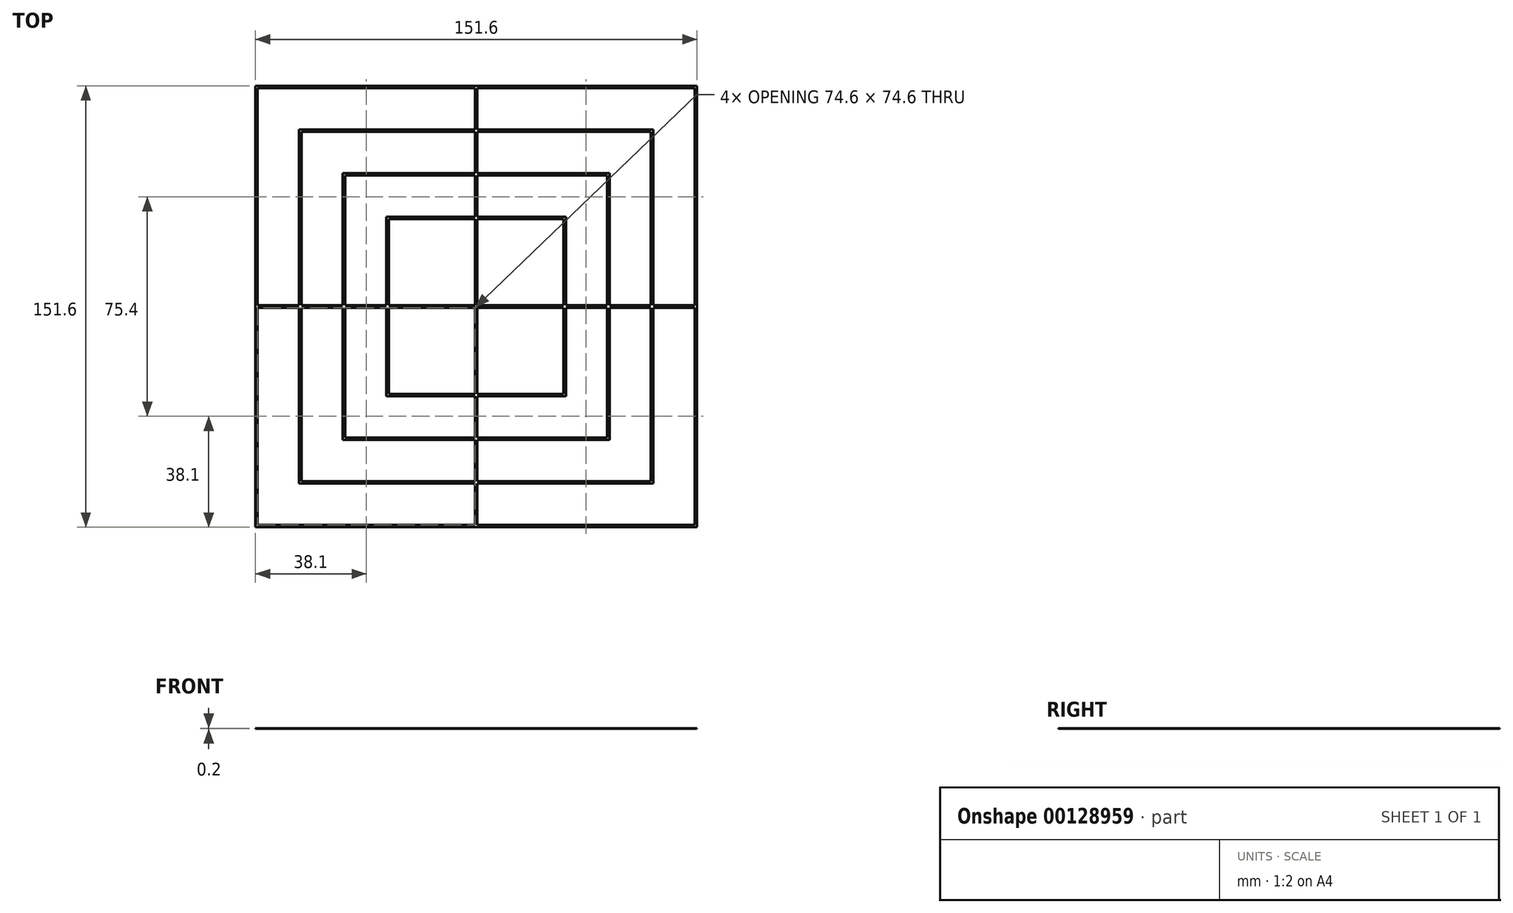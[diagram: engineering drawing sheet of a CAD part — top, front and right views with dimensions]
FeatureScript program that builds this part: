
annotation { "Feature Type Name" : "Feature", "Feature Type Description" : "" }
export const myFeature = defineFeature(function(context is Context, id is Id, definition is map)
    precondition{}
    {
        {
            var Q0;
            Q0=qCreatedBy(makeId("Top.planeOp"),FACE);
            var sketch = newSketch(context, id + "F0", { "sketchPlane" : qUnion([Q0])});
            skLineSegment(sketch, "E0.bottom", {"start": v(75, -75) * mm, "end": v(-75, -75) * mm});
            skLineSegment(sketch, "E0.top", {"start": v(75, 75) * mm, "end": v(-75, 75) * mm});
            skLineSegment(sketch, "E0.left", {"start": v(75, -75) * mm, "end": v(75, 75) * mm});
            skLineSegment(sketch, "E0.right", {"start": v(-75, -75) * mm, "end": v(-75, 75) * mm});
            skPoint(sketch, "E0.middle", {"position": v(0, 0) * mm});
            skLineSegment(sketch, "E1.bottom", {"start": v(60, -60) * mm, "end": v(-60, -60) * mm});
            skLineSegment(sketch, "E1.top", {"start": v(60, 60) * mm, "end": v(-60, 60) * mm});
            skLineSegment(sketch, "E1.left", {"start": v(60, -60) * mm, "end": v(60, 60) * mm});
            skLineSegment(sketch, "E1.right", {"start": v(-60, -60) * mm, "end": v(-60, 60) * mm});
            skLineSegment(sketch, "E2.bottom", {"start": v(45, -45) * mm, "end": v(-45, -45) * mm});
            skLineSegment(sketch, "E2.top", {"start": v(45, 45) * mm, "end": v(-45, 45) * mm});
            skLineSegment(sketch, "E2.left", {"start": v(45, -45) * mm, "end": v(45, 45) * mm});
            skLineSegment(sketch, "E2.right", {"start": v(-45, -45) * mm, "end": v(-45, 45) * mm});
            skLineSegment(sketch, "E3.bottom", {"start": v(30, -30) * mm, "end": v(-30, -30) * mm});
            skLineSegment(sketch, "E3.top", {"start": v(30, 30) * mm, "end": v(-30, 30) * mm});
            skLineSegment(sketch, "E3.left", {"start": v(30, -30) * mm, "end": v(30, 30) * mm});
            skLineSegment(sketch, "E3.right", {"start": v(-30, -30) * mm, "end": v(-30, 30) * mm});
            skLineSegment(sketch, "E4", {"start": v(-75, 0) * mm, "end": v(75, 0) * mm});
            skLineSegment(sketch, "E5", {"start": v(0, 75) * mm, "end": v(0, -75) * mm});
            skLineSegment(sketch, "E6.bottom", {"start": v(75.8, -75.8) * mm, "end": v(-75.8, -75.8) * mm});
            skLineSegment(sketch, "E6.top", {"start": v(75.8, 75.8) * mm, "end": v(-75.8, 75.8) * mm});
            skLineSegment(sketch, "E6.left", {"start": v(75.8, -75.8) * mm, "end": v(75.8, 75.8) * mm});
            skLineSegment(sketch, "E6.right", {"start": v(-75.8, -75.8) * mm, "end": v(-75.8, 75.8) * mm});
            skLineSegment(sketch, "E7.bottom", {"start": v(60.8, -60.8) * mm, "end": v(-60.8, -60.8) * mm});
            skLineSegment(sketch, "E7.top", {"start": v(60.8, 60.8) * mm, "end": v(-60.8, 60.8) * mm});
            skLineSegment(sketch, "E7.left", {"start": v(60.8, -60.8) * mm, "end": v(60.8, 60.8) * mm});
            skLineSegment(sketch, "E7.right", {"start": v(-60.8, -60.8) * mm, "end": v(-60.8, 60.8) * mm});
            skLineSegment(sketch, "E8.bottom", {"start": v(45.8, -45.8) * mm, "end": v(-45.8, -45.8) * mm});
            skLineSegment(sketch, "E8.top", {"start": v(45.8, 45.8) * mm, "end": v(-45.8, 45.8) * mm});
            skLineSegment(sketch, "E8.left", {"start": v(45.8, -45.8) * mm, "end": v(45.8, 45.8) * mm});
            skLineSegment(sketch, "E8.right", {"start": v(-45.8, -45.8) * mm, "end": v(-45.8, 45.8) * mm});
            skLineSegment(sketch, "E9.bottom", {"start": v(30.8, -30.8) * mm, "end": v(-30.8, -30.8) * mm});
            skLineSegment(sketch, "E9.top", {"start": v(30.8, 30.8) * mm, "end": v(-30.8, 30.8) * mm});
            skLineSegment(sketch, "E9.left", {"start": v(30.8, -30.8) * mm, "end": v(30.8, 30.8) * mm});
            skLineSegment(sketch, "E9.right", {"start": v(-30.8, -30.8) * mm, "end": v(-30.8, 30.8) * mm});
            skLineSegment(sketch, "E10", {"start": v(-75, -0.4) * mm, "end": v(75, -0.4) * mm});
            skLineSegment(sketch, "E11.MirrorCS", {"start": v(-75, 0.4) * mm, "end": v(75, 0.4) * mm});
            skLineSegment(sketch, "E12", {"start": v(-0.4, 75) * mm, "end": v(-0.4, -75) * mm});
            skLineSegment(sketch, "E13.MirrorCS", {"start": v(0.4, 75) * mm, "end": v(0.4, -75) * mm});
            skSolve(sketch);
        }
        {
            var Q0;
            {var subQ5=sQuery(id+"F0.wireOp",EDGE,"E3.right");var subQ6=sQuery(id+"F0.wireOp",EDGE,"E3.top");var subQ7=makeQuery(id+"F0.imprint","INTERSECT",VERTEX,{"derivedFrom":[subQ6,subQ5]});Q0=makeQuery(id+"F0.imprint","IMPRINT",FACE,{"disambiguationData":[TD([[makeQuery(id+"F0.imprint","IMPRINT",EDGE,{"disambiguationData":[TD([[subQ7,1.0]])],"derivedFrom":subQ6}),-1.0]])]});}
            var Q1;
            {var subQ6=sQuery(id+"F0.wireOp",EDGE,"E1.right");var subQ9=sQuery(id+"F0.wireOp",EDGE,"E1.top");var subQ10=makeQuery(id+"F0.imprint","INTERSECT",VERTEX,{"derivedFrom":[subQ9,subQ6]});Q1=makeQuery(id+"F0.imprint","IMPRINT",FACE,{"disambiguationData":[TD([[makeQuery(id+"F0.imprint","IMPRINT",EDGE,{"disambiguationData":[TD([[subQ10,1.0]])],"derivedFrom":subQ9}),-1.0]])]});}
            var Q2;
            {var subQ5=sQuery(id+"F0.wireOp",EDGE,"E2.right");var subQ6=sQuery(id+"F0.wireOp",EDGE,"E2.top");var subQ7=makeQuery(id+"F0.imprint","INTERSECT",VERTEX,{"derivedFrom":[subQ6,subQ5]});Q2=makeQuery(id+"F0.imprint","IMPRINT",FACE,{"disambiguationData":[TD([[makeQuery(id+"F0.imprint","IMPRINT",EDGE,{"disambiguationData":[TD([[subQ7,1.0]])],"derivedFrom":subQ6}),-1.0]])]});}
            var Q3;
            {var subQ5=sQuery(id+"F0.wireOp",EDGE,"E3.right");var subQ6=sQuery(id+"F0.wireOp",EDGE,"E3.bottom");var subQ7=makeQuery(id+"F0.imprint","INTERSECT",VERTEX,{"derivedFrom":[subQ6,subQ5]});Q3=makeQuery(id+"F0.imprint","IMPRINT",FACE,{"disambiguationData":[TD([[makeQuery(id+"F0.imprint","IMPRINT",EDGE,{"disambiguationData":[TD([[subQ7,1.0]])],"derivedFrom":subQ6}),1.0]])]});}
            var Q4;
            {var subQ7=sQuery(id+"F0.wireOp",EDGE,"E3.left");var subQ8=sQuery(id+"F0.wireOp",EDGE,"E3.top");var subQ9=makeQuery(id+"F0.imprint","INTERSECT",VERTEX,{"derivedFrom":[subQ8,subQ7]});Q4=makeQuery(id+"F0.imprint","IMPRINT",FACE,{"disambiguationData":[TD([[makeQuery(id+"F0.imprint","IMPRINT",EDGE,{"disambiguationData":[TD([[subQ9,-1.0]])],"derivedFrom":subQ8}),-1.0]])]});}
            var Q5;
            {var subQ7=sQuery(id+"F0.wireOp",EDGE,"E2.left");var subQ9=sQuery(id+"F0.wireOp",EDGE,"E2.top");var subQ10=makeQuery(id+"F0.imprint","INTERSECT",VERTEX,{"derivedFrom":[subQ9,subQ7]});Q5=makeQuery(id+"F0.imprint","IMPRINT",FACE,{"disambiguationData":[TD([[makeQuery(id+"F0.imprint","IMPRINT",EDGE,{"disambiguationData":[TD([[subQ10,-1.0]])],"derivedFrom":subQ9}),-1.0]])]});}
            var Q6;
            {var subQ7=sQuery(id+"F0.wireOp",EDGE,"E3.left");var subQ8=sQuery(id+"F0.wireOp",EDGE,"E3.bottom");var subQ9=makeQuery(id+"F0.imprint","INTERSECT",VERTEX,{"derivedFrom":[subQ8,subQ7]});Q6=makeQuery(id+"F0.imprint","IMPRINT",FACE,{"disambiguationData":[TD([[makeQuery(id+"F0.imprint","IMPRINT",EDGE,{"disambiguationData":[TD([[subQ9,-1.0]])],"derivedFrom":subQ8}),1.0]])]});}
            var Q7;
            {var subQ5=sQuery(id+"F0.wireOp",EDGE,"E1.left");var subQ6=sQuery(id+"F0.wireOp",EDGE,"E1.bottom");var subQ7=makeQuery(id+"F0.imprint","INTERSECT",VERTEX,{"derivedFrom":[subQ6,subQ5]});Q7=makeQuery(id+"F0.imprint","IMPRINT",FACE,{"disambiguationData":[TD([[makeQuery(id+"F0.imprint","IMPRINT",EDGE,{"disambiguationData":[TD([[subQ7,-1.0]])],"derivedFrom":subQ6}),1.0]])]});}
            var Q8;
            {var subQ0=sQuery(id+"F0.wireOp",EDGE,"E1.right");var subQ1=sQuery(id+"F0.wireOp",EDGE,"E1.bottom");var subQ2=makeQuery(id+"F0.imprint","INTERSECT",VERTEX,{"derivedFrom":[subQ1,subQ0]});Q8=makeQuery(id+"F0.imprint","IMPRINT",FACE,{"disambiguationData":[TD([[makeQuery(id+"F0.imprint","IMPRINT",EDGE,{"disambiguationData":[TD([[subQ2,1.0]])],"derivedFrom":subQ1}),1.0]])]});}
            var Q9;
            Q9=makeQuery(id+"F0.imprint","IMPRINT",FACE,{"disambiguationData":[TD([[makeQuery(id+"F0.imprint","IMPRINT",EDGE,{"derivedFrom":sQuery(id+"F0.wireOp",EDGE,"E6.bottom")}),-1.0]])]});
            var Q10;
            {var subQ7=sQuery(id+"F0.wireOp",EDGE,"E1.left");var subQ8=sQuery(id+"F0.wireOp",EDGE,"E1.top");var subQ9=makeQuery(id+"F0.imprint","INTERSECT",VERTEX,{"derivedFrom":[subQ8,subQ7]});Q10=makeQuery(id+"F0.imprint","IMPRINT",FACE,{"disambiguationData":[TD([[makeQuery(id+"F0.imprint","IMPRINT",EDGE,{"disambiguationData":[TD([[subQ9,-1.0]])],"derivedFrom":subQ8}),-1.0]])]});}
            var Q11;
            {var subQ0=sQuery(id+"F0.wireOp",EDGE,"E10");var subQ1=sQuery(id+"F0.wireOp",EDGE,"E1.right");var subQ2=makeQuery(id+"F0.imprint","INTERSECT",VERTEX,{"derivedFrom":[subQ1,subQ0]});Q11=makeQuery(id+"F0.imprint","IMPRINT",FACE,{"disambiguationData":[TD([[makeQuery(id+"F0.imprint","IMPRINT",EDGE,{"disambiguationData":[TD([[subQ2,-1.0]])],"derivedFrom":subQ1}),-1.0]])]});}
            var Q12;
            {var subQ0=sQuery(id+"F0.wireOp",EDGE,"E4");var subQ1=sQuery(id+"F0.wireOp",EDGE,"E3.left");var subQ2=makeQuery(id+"F0.imprint","INTERSECT",VERTEX,{"derivedFrom":[subQ1,subQ0]});Q12=makeQuery(id+"F0.imprint","IMPRINT",FACE,{"disambiguationData":[TD([[makeQuery(id+"F0.imprint","IMPRINT",EDGE,{"disambiguationData":[TD([[subQ2,-1.0]])],"derivedFrom":subQ1}),1.0]])]});}
            var Q13;
            {var subQ5=sQuery(id+"F0.wireOp",EDGE,"E2.right");var subQ6=sQuery(id+"F0.wireOp",EDGE,"E2.bottom");var subQ7=makeQuery(id+"F0.imprint","INTERSECT",VERTEX,{"derivedFrom":[subQ6,subQ5]});Q13=makeQuery(id+"F0.imprint","IMPRINT",FACE,{"disambiguationData":[TD([[makeQuery(id+"F0.imprint","IMPRINT",EDGE,{"disambiguationData":[TD([[subQ7,1.0]])],"derivedFrom":subQ6}),1.0]])]});}
            var Q14;
            {var subQ0=sQuery(id+"F0.wireOp",EDGE,"E4");var subQ1=sQuery(id+"F0.wireOp",EDGE,"E2.right");var subQ2=makeQuery(id+"F0.imprint","INTERSECT",VERTEX,{"derivedFrom":[subQ1,subQ0]});Q14=makeQuery(id+"F0.imprint","IMPRINT",FACE,{"disambiguationData":[TD([[makeQuery(id+"F0.imprint","IMPRINT",EDGE,{"disambiguationData":[TD([[subQ2,-1.0]])],"derivedFrom":subQ1}),1.0]])]});}
            var Q15;
            {var subQ0=sQuery(id+"F0.wireOp",EDGE,"E10");var subQ1=sQuery(id+"F0.wireOp",EDGE,"E1.left");var subQ2=makeQuery(id+"F0.imprint","INTERSECT",VERTEX,{"derivedFrom":[subQ1,subQ0]});Q15=makeQuery(id+"F0.imprint","IMPRINT",FACE,{"disambiguationData":[TD([[makeQuery(id+"F0.imprint","IMPRINT",EDGE,{"disambiguationData":[TD([[subQ2,-1.0]])],"derivedFrom":subQ1}),1.0]])]});}
            var Q16;
            {var subQ0=sQuery(id+"F0.wireOp",EDGE,"E10");var subQ1=sQuery(id+"F0.wireOp",EDGE,"E1.right");var subQ2=makeQuery(id+"F0.imprint","INTERSECT",VERTEX,{"derivedFrom":[subQ1,subQ0]});Q16=makeQuery(id+"F0.imprint","IMPRINT",FACE,{"disambiguationData":[TD([[makeQuery(id+"F0.imprint","IMPRINT",EDGE,{"disambiguationData":[TD([[subQ2,-1.0]])],"derivedFrom":subQ1}),1.0]])]});}
            var Q17;
            {var subQ0=sQuery(id+"F0.wireOp",EDGE,"E10");var subQ1=sQuery(id+"F0.wireOp",EDGE,"E2.right");var subQ2=makeQuery(id+"F0.imprint","INTERSECT",VERTEX,{"derivedFrom":[subQ1,subQ0]});Q17=makeQuery(id+"F0.imprint","IMPRINT",FACE,{"disambiguationData":[TD([[makeQuery(id+"F0.imprint","IMPRINT",EDGE,{"disambiguationData":[TD([[subQ2,-1.0]])],"derivedFrom":subQ1}),-1.0]])]});}
            var Q18;
            {var subQ0=sQuery(id+"F0.wireOp",EDGE,"E4");var subQ1=sQuery(id+"F0.wireOp",EDGE,"E0.left");var subQ2=makeQuery(id+"F0.imprint","INTERSECT",VERTEX,{"derivedFrom":[subQ1,subQ0]});Q18=makeQuery(id+"F0.imprint","IMPRINT",FACE,{"disambiguationData":[TD([[makeQuery(id+"F0.imprint","IMPRINT",EDGE,{"disambiguationData":[TD([[subQ2,-1.0]])],"derivedFrom":subQ1}),1.0]])]});}
            var Q19;
            {var subQ0=sQuery(id+"F0.wireOp",EDGE,"E4");var subQ1=sQuery(id+"F0.wireOp",EDGE,"E0.right");var subQ2=makeQuery(id+"F0.imprint","INTERSECT",VERTEX,{"derivedFrom":[subQ1,subQ0]});Q19=makeQuery(id+"F0.imprint","IMPRINT",FACE,{"disambiguationData":[TD([[makeQuery(id+"F0.imprint","IMPRINT",EDGE,{"disambiguationData":[TD([[subQ2,-1.0]])],"derivedFrom":subQ1}),-1.0]])]});}
            var Q20;
            {var subQ0=sQuery(id+"F0.wireOp",EDGE,"E10");var subQ1=sQuery(id+"F0.wireOp",EDGE,"E3.left");var subQ2=makeQuery(id+"F0.imprint","INTERSECT",VERTEX,{"derivedFrom":[subQ1,subQ0]});Q20=makeQuery(id+"F0.imprint","IMPRINT",FACE,{"disambiguationData":[TD([[makeQuery(id+"F0.imprint","IMPRINT",EDGE,{"disambiguationData":[TD([[subQ2,-1.0]])],"derivedFrom":subQ1}),-1.0]])]});}
            var Q21;
            {var subQ0=sQuery(id+"F0.wireOp",EDGE,"E4");var subQ1=sQuery(id+"F0.wireOp",EDGE,"E1.right");var subQ2=makeQuery(id+"F0.imprint","INTERSECT",VERTEX,{"derivedFrom":[subQ1,subQ0]});Q21=makeQuery(id+"F0.imprint","IMPRINT",FACE,{"disambiguationData":[TD([[makeQuery(id+"F0.imprint","IMPRINT",EDGE,{"disambiguationData":[TD([[subQ2,-1.0]])],"derivedFrom":subQ1}),1.0]])]});}
            var Q22;
            {var subQ0=sQuery(id+"F0.wireOp",EDGE,"E4");var subQ1=sQuery(id+"F0.wireOp",EDGE,"E1.right");var subQ2=makeQuery(id+"F0.imprint","INTERSECT",VERTEX,{"derivedFrom":[subQ1,subQ0]});Q22=makeQuery(id+"F0.imprint","IMPRINT",FACE,{"disambiguationData":[TD([[makeQuery(id+"F0.imprint","IMPRINT",EDGE,{"disambiguationData":[TD([[subQ2,-1.0]])],"derivedFrom":subQ1}),-1.0]])]});}
            var Q23;
            {var subQ0=sQuery(id+"F0.wireOp",EDGE,"E4");var subQ1=sQuery(id+"F0.wireOp",EDGE,"E2.left");var subQ2=makeQuery(id+"F0.imprint","INTERSECT",VERTEX,{"derivedFrom":[subQ1,subQ0]});Q23=makeQuery(id+"F0.imprint","IMPRINT",FACE,{"disambiguationData":[TD([[makeQuery(id+"F0.imprint","IMPRINT",EDGE,{"disambiguationData":[TD([[subQ2,-1.0]])],"derivedFrom":subQ1}),1.0]])]});}
            var Q24;
            {var subQ0=sQuery(id+"F0.wireOp",EDGE,"E4");var subQ1=sQuery(id+"F0.wireOp",EDGE,"E1.left");var subQ2=makeQuery(id+"F0.imprint","INTERSECT",VERTEX,{"derivedFrom":[subQ1,subQ0]});Q24=makeQuery(id+"F0.imprint","IMPRINT",FACE,{"disambiguationData":[TD([[makeQuery(id+"F0.imprint","IMPRINT",EDGE,{"disambiguationData":[TD([[subQ2,-1.0]])],"derivedFrom":subQ1}),-1.0]])]});}
            var Q25;
            {var subQ0=sQuery(id+"F0.wireOp",EDGE,"E4");var subQ1=sQuery(id+"F0.wireOp",EDGE,"E3.right");var subQ2=makeQuery(id+"F0.imprint","INTERSECT",VERTEX,{"derivedFrom":[subQ1,subQ0]});Q25=makeQuery(id+"F0.imprint","IMPRINT",FACE,{"disambiguationData":[TD([[makeQuery(id+"F0.imprint","IMPRINT",EDGE,{"disambiguationData":[TD([[subQ2,-1.0]])],"derivedFrom":subQ1}),-1.0]])]});}
            var Q26;
            {var subQ5=sQuery(id+"F0.wireOp",EDGE,"E2.left");var subQ6=sQuery(id+"F0.wireOp",EDGE,"E2.bottom");var subQ7=makeQuery(id+"F0.imprint","INTERSECT",VERTEX,{"derivedFrom":[subQ6,subQ5]});Q26=makeQuery(id+"F0.imprint","IMPRINT",FACE,{"disambiguationData":[TD([[makeQuery(id+"F0.imprint","IMPRINT",EDGE,{"disambiguationData":[TD([[subQ7,-1.0]])],"derivedFrom":subQ6}),1.0]])]});}
            var Q27;
            {var subQ0=sQuery(id+"F0.wireOp",EDGE,"E4");var subQ1=sQuery(id+"F0.wireOp",EDGE,"E1.left");var subQ2=makeQuery(id+"F0.imprint","INTERSECT",VERTEX,{"derivedFrom":[subQ1,subQ0]});Q27=makeQuery(id+"F0.imprint","IMPRINT",FACE,{"disambiguationData":[TD([[makeQuery(id+"F0.imprint","IMPRINT",EDGE,{"disambiguationData":[TD([[subQ2,-1.0]])],"derivedFrom":subQ1}),1.0]])]});}
            var Q28;
            {var subQ0=sQuery(id+"F0.wireOp",EDGE,"E4");var subQ1=sQuery(id+"F0.wireOp",EDGE,"E2.right");var subQ2=makeQuery(id+"F0.imprint","INTERSECT",VERTEX,{"derivedFrom":[subQ1,subQ0]});Q28=makeQuery(id+"F0.imprint","IMPRINT",FACE,{"disambiguationData":[TD([[makeQuery(id+"F0.imprint","IMPRINT",EDGE,{"disambiguationData":[TD([[subQ2,-1.0]])],"derivedFrom":subQ1}),-1.0]])]});}
            var Q29;
            {var subQ0=sQuery(id+"F0.wireOp",EDGE,"E5");var subQ1=sQuery(id+"F0.wireOp",EDGE,"E0.bottom");var subQ2=makeQuery(id+"F0.imprint","INTERSECT",VERTEX,{"derivedFrom":[subQ1,subQ0]});Q29=makeQuery(id+"F0.imprint","IMPRINT",FACE,{"disambiguationData":[TD([[makeQuery(id+"F0.imprint","IMPRINT",EDGE,{"disambiguationData":[TD([[subQ2,1.0]])],"derivedFrom":subQ1}),-1.0]])]});}
            var Q30;
            {var subQ0=sQuery(id+"F0.wireOp",EDGE,"E4");var subQ1=sQuery(id+"F0.wireOp",EDGE,"E2.left");var subQ2=makeQuery(id+"F0.imprint","INTERSECT",VERTEX,{"derivedFrom":[subQ1,subQ0]});Q30=makeQuery(id+"F0.imprint","IMPRINT",FACE,{"disambiguationData":[TD([[makeQuery(id+"F0.imprint","IMPRINT",EDGE,{"disambiguationData":[TD([[subQ2,-1.0]])],"derivedFrom":subQ1}),-1.0]])]});}
            var Q31;
            {var subQ0=sQuery(id+"F0.wireOp",EDGE,"E10");var subQ1=sQuery(id+"F0.wireOp",EDGE,"E2.right");var subQ2=makeQuery(id+"F0.imprint","INTERSECT",VERTEX,{"derivedFrom":[subQ1,subQ0]});Q31=makeQuery(id+"F0.imprint","IMPRINT",FACE,{"disambiguationData":[TD([[makeQuery(id+"F0.imprint","IMPRINT",EDGE,{"disambiguationData":[TD([[subQ2,-1.0]])],"derivedFrom":subQ1}),1.0]])]});}
            var Q32;
            {var subQ0=sQuery(id+"F0.wireOp",EDGE,"E10");var subQ1=sQuery(id+"F0.wireOp",EDGE,"E3.left");var subQ2=makeQuery(id+"F0.imprint","INTERSECT",VERTEX,{"derivedFrom":[subQ1,subQ0]});Q32=makeQuery(id+"F0.imprint","IMPRINT",FACE,{"disambiguationData":[TD([[makeQuery(id+"F0.imprint","IMPRINT",EDGE,{"disambiguationData":[TD([[subQ2,-1.0]])],"derivedFrom":subQ1}),1.0]])]});}
            var Q33;
            {var subQ0=sQuery(id+"F0.wireOp",EDGE,"E10");var subQ1=sQuery(id+"F0.wireOp",EDGE,"E3.right");var subQ2=makeQuery(id+"F0.imprint","INTERSECT",VERTEX,{"derivedFrom":[subQ1,subQ0]});Q33=makeQuery(id+"F0.imprint","IMPRINT",FACE,{"disambiguationData":[TD([[makeQuery(id+"F0.imprint","IMPRINT",EDGE,{"disambiguationData":[TD([[subQ2,-1.0]])],"derivedFrom":subQ1}),1.0]])]});}
            var Q34;
            {var subQ0=sQuery(id+"F0.wireOp",EDGE,"E4");var subQ1=sQuery(id+"F0.wireOp",EDGE,"E0.right");var subQ2=makeQuery(id+"F0.imprint","INTERSECT",VERTEX,{"derivedFrom":[subQ1,subQ0]});Q34=makeQuery(id+"F0.imprint","IMPRINT",FACE,{"disambiguationData":[TD([[makeQuery(id+"F0.imprint","IMPRINT",EDGE,{"disambiguationData":[TD([[subQ2,1.0]])],"derivedFrom":subQ1}),-1.0]])]});}
            var Q35;
            {var subQ0=sQuery(id+"F0.wireOp",EDGE,"E5");var subQ1=sQuery(id+"F0.wireOp",EDGE,"E1.top");var subQ2=makeQuery(id+"F0.imprint","INTERSECT",VERTEX,{"derivedFrom":[subQ1,subQ0]});Q35=makeQuery(id+"F0.imprint","IMPRINT",FACE,{"disambiguationData":[TD([[makeQuery(id+"F0.imprint","IMPRINT",EDGE,{"disambiguationData":[TD([[subQ2,-1.0]])],"derivedFrom":subQ1}),1.0]])]});}
            var Q36;
            {var subQ0=sQuery(id+"F0.wireOp",EDGE,"E5");var subQ1=sQuery(id+"F0.wireOp",EDGE,"E2.top");var subQ2=makeQuery(id+"F0.imprint","INTERSECT",VERTEX,{"derivedFrom":[subQ1,subQ0]});Q36=makeQuery(id+"F0.imprint","IMPRINT",FACE,{"disambiguationData":[TD([[makeQuery(id+"F0.imprint","IMPRINT",EDGE,{"disambiguationData":[TD([[subQ2,-1.0]])],"derivedFrom":subQ1}),-1.0]])]});}
            var Q37;
            {var subQ0=sQuery(id+"F0.wireOp",EDGE,"E5");var subQ1=sQuery(id+"F0.wireOp",EDGE,"E3.bottom");var subQ2=makeQuery(id+"F0.imprint","INTERSECT",VERTEX,{"derivedFrom":[subQ1,subQ0]});Q37=makeQuery(id+"F0.imprint","IMPRINT",FACE,{"disambiguationData":[TD([[makeQuery(id+"F0.imprint","IMPRINT",EDGE,{"disambiguationData":[TD([[subQ2,-1.0]])],"derivedFrom":subQ1}),1.0]])]});}
            var Q38;
            {var subQ0=sQuery(id+"F0.wireOp",EDGE,"E5");var subQ1=sQuery(id+"F0.wireOp",EDGE,"E1.bottom");var subQ2=makeQuery(id+"F0.imprint","INTERSECT",VERTEX,{"derivedFrom":[subQ1,subQ0]});Q38=makeQuery(id+"F0.imprint","IMPRINT",FACE,{"disambiguationData":[TD([[makeQuery(id+"F0.imprint","IMPRINT",EDGE,{"disambiguationData":[TD([[subQ2,-1.0]])],"derivedFrom":subQ1}),-1.0]])]});}
            var Q39;
            {var subQ0=sQuery(id+"F0.wireOp",EDGE,"E5");var subQ1=sQuery(id+"F0.wireOp",EDGE,"E3.top");var subQ2=makeQuery(id+"F0.imprint","INTERSECT",VERTEX,{"derivedFrom":[subQ1,subQ0]});Q39=makeQuery(id+"F0.imprint","IMPRINT",FACE,{"disambiguationData":[TD([[makeQuery(id+"F0.imprint","IMPRINT",EDGE,{"disambiguationData":[TD([[subQ2,-1.0]])],"derivedFrom":subQ1}),1.0]])]});}
            var Q40;
            {var subQ0=sQuery(id+"F0.wireOp",EDGE,"E5");var subQ1=sQuery(id+"F0.wireOp",EDGE,"E0.top");var subQ2=makeQuery(id+"F0.imprint","INTERSECT",VERTEX,{"derivedFrom":[subQ1,subQ0]});Q40=makeQuery(id+"F0.imprint","IMPRINT",FACE,{"disambiguationData":[TD([[makeQuery(id+"F0.imprint","IMPRINT",EDGE,{"disambiguationData":[TD([[subQ2,1.0]])],"derivedFrom":subQ1}),1.0]])]});}
            var Q41;
            {var subQ0=sQuery(id+"F0.wireOp",EDGE,"E4");var subQ1=sQuery(id+"F0.wireOp",EDGE,"E0.left");var subQ2=makeQuery(id+"F0.imprint","INTERSECT",VERTEX,{"derivedFrom":[subQ1,subQ0]});Q41=makeQuery(id+"F0.imprint","IMPRINT",FACE,{"disambiguationData":[TD([[makeQuery(id+"F0.imprint","IMPRINT",EDGE,{"disambiguationData":[TD([[subQ2,1.0]])],"derivedFrom":subQ1}),1.0]])]});}
            var Q42;
            {var subQ0=sQuery(id+"F0.wireOp",EDGE,"E10");var subQ1=sQuery(id+"F0.wireOp",EDGE,"E3.right");var subQ2=makeQuery(id+"F0.imprint","INTERSECT",VERTEX,{"derivedFrom":[subQ1,subQ0]});Q42=makeQuery(id+"F0.imprint","IMPRINT",FACE,{"disambiguationData":[TD([[makeQuery(id+"F0.imprint","IMPRINT",EDGE,{"disambiguationData":[TD([[subQ2,-1.0]])],"derivedFrom":subQ1}),-1.0]])]});}
            var Q43;
            {var subQ0=sQuery(id+"F0.wireOp",EDGE,"E10");var subQ1=sQuery(id+"F0.wireOp",EDGE,"E1.left");var subQ2=makeQuery(id+"F0.imprint","INTERSECT",VERTEX,{"derivedFrom":[subQ1,subQ0]});Q43=makeQuery(id+"F0.imprint","IMPRINT",FACE,{"disambiguationData":[TD([[makeQuery(id+"F0.imprint","IMPRINT",EDGE,{"disambiguationData":[TD([[subQ2,-1.0]])],"derivedFrom":subQ1}),-1.0]])]});}
            var Q44;
            {var subQ0=sQuery(id+"F0.wireOp",EDGE,"E13.MirrorCS");var subQ1=sQuery(id+"F0.wireOp",EDGE,"E1.top");var subQ2=makeQuery(id+"F0.imprint","INTERSECT",VERTEX,{"derivedFrom":[subQ1,subQ0]});Q44=makeQuery(id+"F0.imprint","IMPRINT",FACE,{"disambiguationData":[TD([[makeQuery(id+"F0.imprint","IMPRINT",EDGE,{"disambiguationData":[TD([[subQ2,-1.0]])],"derivedFrom":subQ1}),-1.0]])]});}
            var Q45;
            {var subQ0=sQuery(id+"F0.wireOp",EDGE,"E13.MirrorCS");var subQ1=sQuery(id+"F0.wireOp",EDGE,"E2.bottom");var subQ2=makeQuery(id+"F0.imprint","INTERSECT",VERTEX,{"derivedFrom":[subQ1,subQ0]});Q45=makeQuery(id+"F0.imprint","IMPRINT",FACE,{"disambiguationData":[TD([[makeQuery(id+"F0.imprint","IMPRINT",EDGE,{"disambiguationData":[TD([[subQ2,-1.0]])],"derivedFrom":subQ1}),-1.0]])]});}
            var Q46;
            {var subQ0=sQuery(id+"F0.wireOp",EDGE,"E13.MirrorCS");var subQ1=sQuery(id+"F0.wireOp",EDGE,"E2.top");var subQ2=makeQuery(id+"F0.imprint","INTERSECT",VERTEX,{"derivedFrom":[subQ1,subQ0]});Q46=makeQuery(id+"F0.imprint","IMPRINT",FACE,{"disambiguationData":[TD([[makeQuery(id+"F0.imprint","IMPRINT",EDGE,{"disambiguationData":[TD([[subQ2,-1.0]])],"derivedFrom":subQ1}),1.0]])]});}
            var Q47;
            {var subQ0=sQuery(id+"F0.wireOp",EDGE,"E5");var subQ1=sQuery(id+"F0.wireOp",EDGE,"E3.bottom");var subQ2=makeQuery(id+"F0.imprint","INTERSECT",VERTEX,{"derivedFrom":[subQ1,subQ0]});Q47=makeQuery(id+"F0.imprint","IMPRINT",FACE,{"disambiguationData":[TD([[makeQuery(id+"F0.imprint","IMPRINT",EDGE,{"disambiguationData":[TD([[subQ2,-1.0]])],"derivedFrom":subQ1}),-1.0]])]});}
            var Q48;
            {var subQ0=sQuery(id+"F0.wireOp",EDGE,"E13.MirrorCS");var subQ1=sQuery(id+"F0.wireOp",EDGE,"E1.bottom");var subQ2=makeQuery(id+"F0.imprint","INTERSECT",VERTEX,{"derivedFrom":[subQ1,subQ0]});Q48=makeQuery(id+"F0.imprint","IMPRINT",FACE,{"disambiguationData":[TD([[makeQuery(id+"F0.imprint","IMPRINT",EDGE,{"disambiguationData":[TD([[subQ2,-1.0]])],"derivedFrom":subQ1}),1.0]])]});}
            var Q49;
            {var subQ0=sQuery(id+"F0.wireOp",EDGE,"E10");var subQ1=sQuery(id+"F0.wireOp",EDGE,"E2.left");var subQ2=makeQuery(id+"F0.imprint","INTERSECT",VERTEX,{"derivedFrom":[subQ1,subQ0]});Q49=makeQuery(id+"F0.imprint","IMPRINT",FACE,{"disambiguationData":[TD([[makeQuery(id+"F0.imprint","IMPRINT",EDGE,{"disambiguationData":[TD([[subQ2,-1.0]])],"derivedFrom":subQ1}),1.0]])]});}
            var Q50;
            {var subQ0=sQuery(id+"F0.wireOp",EDGE,"E4");var subQ1=sQuery(id+"F0.wireOp",EDGE,"E3.right");var subQ2=makeQuery(id+"F0.imprint","INTERSECT",VERTEX,{"derivedFrom":[subQ1,subQ0]});Q50=makeQuery(id+"F0.imprint","IMPRINT",FACE,{"disambiguationData":[TD([[makeQuery(id+"F0.imprint","IMPRINT",EDGE,{"disambiguationData":[TD([[subQ2,-1.0]])],"derivedFrom":subQ1}),1.0]])]});}
            var Q51;
            {var subQ0=sQuery(id+"F0.wireOp",EDGE,"E4");var subQ1=sQuery(id+"F0.wireOp",EDGE,"E3.left");var subQ2=makeQuery(id+"F0.imprint","INTERSECT",VERTEX,{"derivedFrom":[subQ1,subQ0]});Q51=makeQuery(id+"F0.imprint","IMPRINT",FACE,{"disambiguationData":[TD([[makeQuery(id+"F0.imprint","IMPRINT",EDGE,{"disambiguationData":[TD([[subQ2,-1.0]])],"derivedFrom":subQ1}),-1.0]])]});}
            var Q52;
            {var subQ0=sQuery(id+"F0.wireOp",EDGE,"E5");var subQ1=sQuery(id+"F0.wireOp",EDGE,"E1.bottom");var subQ2=makeQuery(id+"F0.imprint","INTERSECT",VERTEX,{"derivedFrom":[subQ1,subQ0]});Q52=makeQuery(id+"F0.imprint","IMPRINT",FACE,{"disambiguationData":[TD([[makeQuery(id+"F0.imprint","IMPRINT",EDGE,{"disambiguationData":[TD([[subQ2,-1.0]])],"derivedFrom":subQ1}),1.0]])]});}
            var Q53;
            {var subQ0=sQuery(id+"F0.wireOp",EDGE,"E13.MirrorCS");var subQ1=sQuery(id+"F0.wireOp",EDGE,"E1.top");var subQ2=makeQuery(id+"F0.imprint","INTERSECT",VERTEX,{"derivedFrom":[subQ1,subQ0]});Q53=makeQuery(id+"F0.imprint","IMPRINT",FACE,{"disambiguationData":[TD([[makeQuery(id+"F0.imprint","IMPRINT",EDGE,{"disambiguationData":[TD([[subQ2,-1.0]])],"derivedFrom":subQ1}),1.0]])]});}
            var Q54;
            {var subQ0=sQuery(id+"F0.wireOp",EDGE,"E5");var subQ1=sQuery(id+"F0.wireOp",EDGE,"E2.top");var subQ2=makeQuery(id+"F0.imprint","INTERSECT",VERTEX,{"derivedFrom":[subQ1,subQ0]});Q54=makeQuery(id+"F0.imprint","IMPRINT",FACE,{"disambiguationData":[TD([[makeQuery(id+"F0.imprint","IMPRINT",EDGE,{"disambiguationData":[TD([[subQ2,-1.0]])],"derivedFrom":subQ1}),1.0]])]});}
            var Q55;
            {var subQ0=sQuery(id+"F0.wireOp",EDGE,"E5");var subQ1=sQuery(id+"F0.wireOp",EDGE,"E1.top");var subQ2=makeQuery(id+"F0.imprint","INTERSECT",VERTEX,{"derivedFrom":[subQ1,subQ0]});Q55=makeQuery(id+"F0.imprint","IMPRINT",FACE,{"disambiguationData":[TD([[makeQuery(id+"F0.imprint","IMPRINT",EDGE,{"disambiguationData":[TD([[subQ2,-1.0]])],"derivedFrom":subQ1}),-1.0]])]});}
            var Q56;
            {var subQ0=sQuery(id+"F0.wireOp",EDGE,"E5");var subQ1=sQuery(id+"F0.wireOp",EDGE,"E2.bottom");var subQ2=makeQuery(id+"F0.imprint","INTERSECT",VERTEX,{"derivedFrom":[subQ1,subQ0]});Q56=makeQuery(id+"F0.imprint","IMPRINT",FACE,{"disambiguationData":[TD([[makeQuery(id+"F0.imprint","IMPRINT",EDGE,{"disambiguationData":[TD([[subQ2,-1.0]])],"derivedFrom":subQ1}),-1.0]])]});}
            var Q57;
            {var subQ0=sQuery(id+"F0.wireOp",EDGE,"E5");var subQ1=sQuery(id+"F0.wireOp",EDGE,"E2.bottom");var subQ2=makeQuery(id+"F0.imprint","INTERSECT",VERTEX,{"derivedFrom":[subQ1,subQ0]});Q57=makeQuery(id+"F0.imprint","IMPRINT",FACE,{"disambiguationData":[TD([[makeQuery(id+"F0.imprint","IMPRINT",EDGE,{"disambiguationData":[TD([[subQ2,-1.0]])],"derivedFrom":subQ1}),1.0]])]});}
            var Q58;
            {var subQ0=sQuery(id+"F0.wireOp",EDGE,"E5");var subQ1=sQuery(id+"F0.wireOp",EDGE,"E0.bottom");var subQ2=makeQuery(id+"F0.imprint","INTERSECT",VERTEX,{"derivedFrom":[subQ1,subQ0]});Q58=makeQuery(id+"F0.imprint","IMPRINT",FACE,{"disambiguationData":[TD([[makeQuery(id+"F0.imprint","IMPRINT",EDGE,{"disambiguationData":[TD([[subQ2,-1.0]])],"derivedFrom":subQ1}),-1.0]])]});}
            var Q59;
            {var subQ0=sQuery(id+"F0.wireOp",EDGE,"E5");var subQ1=sQuery(id+"F0.wireOp",EDGE,"E0.top");var subQ2=makeQuery(id+"F0.imprint","INTERSECT",VERTEX,{"derivedFrom":[subQ1,subQ0]});Q59=makeQuery(id+"F0.imprint","IMPRINT",FACE,{"disambiguationData":[TD([[makeQuery(id+"F0.imprint","IMPRINT",EDGE,{"disambiguationData":[TD([[subQ2,-1.0]])],"derivedFrom":subQ1}),1.0]])]});}
            var Q60;
            {var subQ0=sQuery(id+"F0.wireOp",EDGE,"E13.MirrorCS");var subQ1=sQuery(id+"F0.wireOp",EDGE,"E3.top");var subQ2=makeQuery(id+"F0.imprint","INTERSECT",VERTEX,{"derivedFrom":[subQ1,subQ0]});Q60=makeQuery(id+"F0.imprint","IMPRINT",FACE,{"disambiguationData":[TD([[makeQuery(id+"F0.imprint","IMPRINT",EDGE,{"disambiguationData":[TD([[subQ2,-1.0]])],"derivedFrom":subQ1}),-1.0]])]});}
            var Q61;
            {var subQ0=sQuery(id+"F0.wireOp",EDGE,"E13.MirrorCS");var subQ1=sQuery(id+"F0.wireOp",EDGE,"E3.bottom");var subQ2=makeQuery(id+"F0.imprint","INTERSECT",VERTEX,{"derivedFrom":[subQ1,subQ0]});Q61=makeQuery(id+"F0.imprint","IMPRINT",FACE,{"disambiguationData":[TD([[makeQuery(id+"F0.imprint","IMPRINT",EDGE,{"disambiguationData":[TD([[subQ2,-1.0]])],"derivedFrom":subQ1}),-1.0]])]});}
            var Q62;
            {var subQ0=sQuery(id+"F0.wireOp",EDGE,"E13.MirrorCS");var subQ1=sQuery(id+"F0.wireOp",EDGE,"E3.top");var subQ2=makeQuery(id+"F0.imprint","INTERSECT",VERTEX,{"derivedFrom":[subQ1,subQ0]});Q62=makeQuery(id+"F0.imprint","IMPRINT",FACE,{"disambiguationData":[TD([[makeQuery(id+"F0.imprint","IMPRINT",EDGE,{"disambiguationData":[TD([[subQ2,-1.0]])],"derivedFrom":subQ1}),1.0]])]});}
            var Q63;
            {var subQ0=sQuery(id+"F0.wireOp",EDGE,"E13.MirrorCS");var subQ1=sQuery(id+"F0.wireOp",EDGE,"E1.bottom");var subQ2=makeQuery(id+"F0.imprint","INTERSECT",VERTEX,{"derivedFrom":[subQ1,subQ0]});Q63=makeQuery(id+"F0.imprint","IMPRINT",FACE,{"disambiguationData":[TD([[makeQuery(id+"F0.imprint","IMPRINT",EDGE,{"disambiguationData":[TD([[subQ2,-1.0]])],"derivedFrom":subQ1}),-1.0]])]});}
            var Q64;
            {var subQ0=sQuery(id+"F0.wireOp",EDGE,"E13.MirrorCS");var subQ1=sQuery(id+"F0.wireOp",EDGE,"E3.bottom");var subQ2=makeQuery(id+"F0.imprint","INTERSECT",VERTEX,{"derivedFrom":[subQ1,subQ0]});Q64=makeQuery(id+"F0.imprint","IMPRINT",FACE,{"disambiguationData":[TD([[makeQuery(id+"F0.imprint","IMPRINT",EDGE,{"disambiguationData":[TD([[subQ2,-1.0]])],"derivedFrom":subQ1}),1.0]])]});}
            var Q65;
            {var subQ0=sQuery(id+"F0.wireOp",EDGE,"E10");var subQ1=sQuery(id+"F0.wireOp",EDGE,"E2.left");var subQ2=makeQuery(id+"F0.imprint","INTERSECT",VERTEX,{"derivedFrom":[subQ1,subQ0]});Q65=makeQuery(id+"F0.imprint","IMPRINT",FACE,{"disambiguationData":[TD([[makeQuery(id+"F0.imprint","IMPRINT",EDGE,{"disambiguationData":[TD([[subQ2,-1.0]])],"derivedFrom":subQ1}),-1.0]])]});}
            var Q66;
            {var subQ0=sQuery(id+"F0.wireOp",EDGE,"E13.MirrorCS");var subQ1=sQuery(id+"F0.wireOp",EDGE,"E2.bottom");var subQ2=makeQuery(id+"F0.imprint","INTERSECT",VERTEX,{"derivedFrom":[subQ1,subQ0]});Q66=makeQuery(id+"F0.imprint","IMPRINT",FACE,{"disambiguationData":[TD([[makeQuery(id+"F0.imprint","IMPRINT",EDGE,{"disambiguationData":[TD([[subQ2,-1.0]])],"derivedFrom":subQ1}),1.0]])]});}
            var Q67;
            {var subQ0=sQuery(id+"F0.wireOp",EDGE,"E13.MirrorCS");var subQ1=sQuery(id+"F0.wireOp",EDGE,"E2.top");var subQ2=makeQuery(id+"F0.imprint","INTERSECT",VERTEX,{"derivedFrom":[subQ1,subQ0]});Q67=makeQuery(id+"F0.imprint","IMPRINT",FACE,{"disambiguationData":[TD([[makeQuery(id+"F0.imprint","IMPRINT",EDGE,{"disambiguationData":[TD([[subQ2,-1.0]])],"derivedFrom":subQ1}),-1.0]])]});}
            var Q68;
            {var subQ0=sQuery(id+"F0.wireOp",EDGE,"E5");var subQ1=sQuery(id+"F0.wireOp",EDGE,"E3.top");var subQ2=makeQuery(id+"F0.imprint","INTERSECT",VERTEX,{"derivedFrom":[subQ1,subQ0]});Q68=makeQuery(id+"F0.imprint","IMPRINT",FACE,{"disambiguationData":[TD([[makeQuery(id+"F0.imprint","IMPRINT",EDGE,{"disambiguationData":[TD([[subQ2,-1.0]])],"derivedFrom":subQ1}),-1.0]])]});}
            var Q69;
            {var subQ0=sQuery(id+"F0.wireOp",EDGE,"E12");var subQ1=sQuery(id+"F0.wireOp",EDGE,"E4");var subQ2=makeQuery(id+"F0.imprint","INTERSECT",VERTEX,{"derivedFrom":[subQ1,subQ0]});Q69=makeQuery(id+"F0.imprint","IMPRINT",FACE,{"disambiguationData":[TD([[makeQuery(id+"F0.imprint","IMPRINT",EDGE,{"disambiguationData":[TD([[subQ2,-1.0]])],"derivedFrom":subQ1}),1.0]])]});}
            var Q70;
            {var subQ0=sQuery(id+"F0.wireOp",EDGE,"E12");var subQ1=sQuery(id+"F0.wireOp",EDGE,"E4");var subQ2=makeQuery(id+"F0.imprint","INTERSECT",VERTEX,{"derivedFrom":[subQ1,subQ0]});Q70=makeQuery(id+"F0.imprint","IMPRINT",FACE,{"disambiguationData":[TD([[makeQuery(id+"F0.imprint","IMPRINT",EDGE,{"disambiguationData":[TD([[subQ2,-1.0]])],"derivedFrom":subQ1}),-1.0]])]});}
            var Q71;
            {var subQ0=sQuery(id+"F0.wireOp",EDGE,"E5");var subQ1=sQuery(id+"F0.wireOp",EDGE,"E4");var subQ2=makeQuery(id+"F0.imprint","INTERSECT",VERTEX,{"derivedFrom":[subQ1,subQ0]});Q71=makeQuery(id+"F0.imprint","IMPRINT",FACE,{"disambiguationData":[TD([[makeQuery(id+"F0.imprint","IMPRINT",EDGE,{"disambiguationData":[TD([[subQ2,-1.0]])],"derivedFrom":subQ1}),1.0]])]});}
            var Q72;
            {var subQ0=sQuery(id+"F0.wireOp",EDGE,"E5");var subQ1=sQuery(id+"F0.wireOp",EDGE,"E4");var subQ2=makeQuery(id+"F0.imprint","INTERSECT",VERTEX,{"derivedFrom":[subQ1,subQ0]});Q72=makeQuery(id+"F0.imprint","IMPRINT",FACE,{"disambiguationData":[TD([[makeQuery(id+"F0.imprint","IMPRINT",EDGE,{"disambiguationData":[TD([[subQ2,-1.0]])],"derivedFrom":subQ1}),-1.0]])]});}
            extrude(context, id + "F1", {"entities" : qUnion([Q0, Q1, Q2, Q3, Q4, Q5, Q6, Q7, Q8, Q9, Q10, Q11, Q12, Q13, Q14, Q15, Q16, Q17, Q18, Q19, Q20, Q21, Q22, Q23, Q24, Q25, Q26, Q27, Q28, Q29, Q30, Q31, Q32, Q33, Q34, Q35, Q36, Q37, Q38, Q39, Q40, Q41, Q42, Q43, Q44, Q45, Q46, Q47, Q48, Q49, Q50, Q51, Q52, Q53, Q54, Q55, Q56, Q57, Q58, Q59, Q60, Q61, Q62, Q63, Q64, Q65, Q66, Q67, Q68, Q69, Q70, Q71, Q72]), "depth" : .2 * mm});
        }
    });
